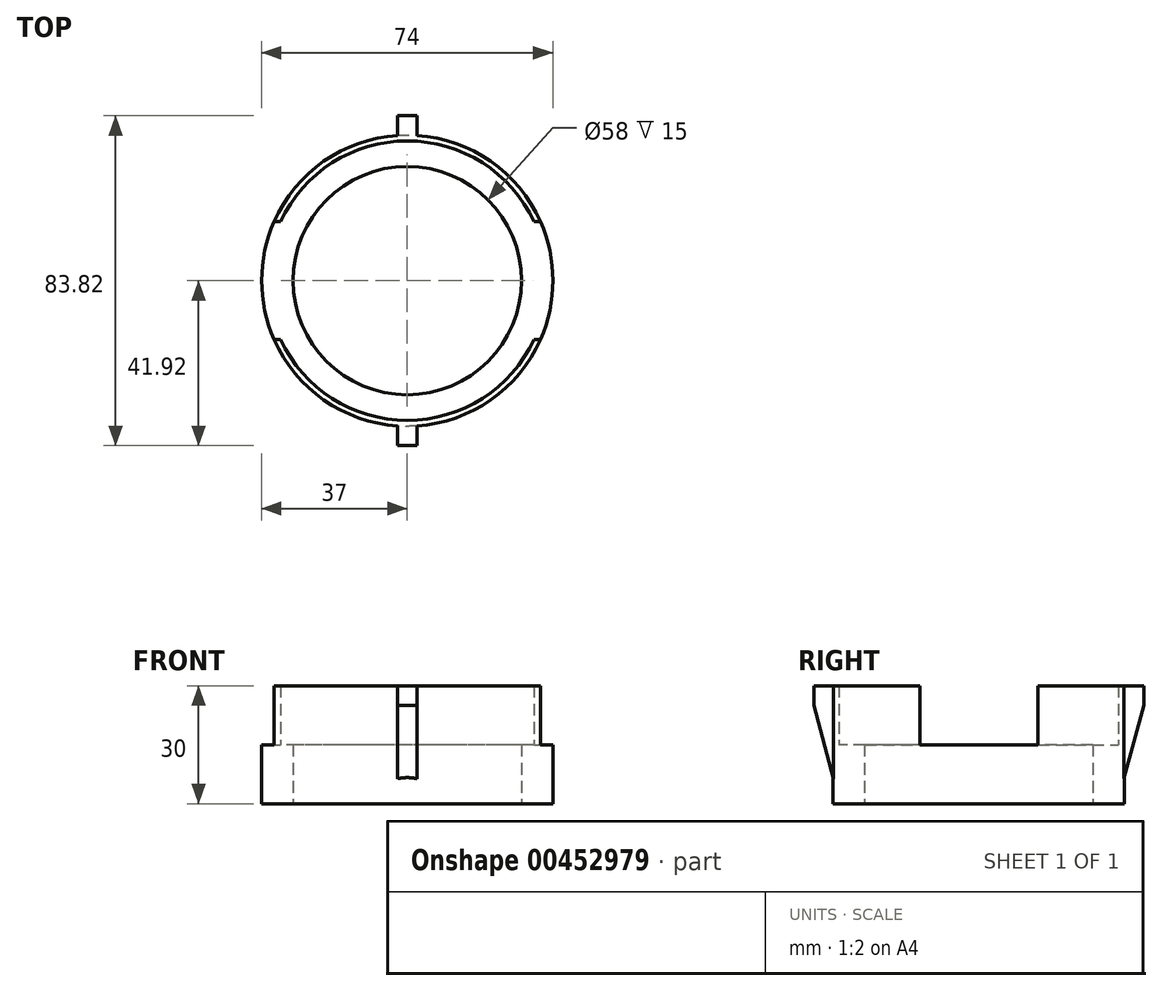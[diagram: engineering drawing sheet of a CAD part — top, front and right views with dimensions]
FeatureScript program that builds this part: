
annotation { "Feature Type Name" : "Feature", "Feature Type Description" : "" }
export const myFeature = defineFeature(function(context is Context, id is Id, definition is map)
    precondition{}
    {
        {
            var Q0;
            Q0=qCreatedBy(makeId("Top.planeOp"),FACE);
            var sketch = newSketch(context, id + "F0", { "sketchPlane" : qUnion([Q0])});
            skCircle(sketch, "E0", {"center": v(0, 0) * mm, "radius": 37 * mm});
            skCircle(sketch, "E1", {"center": v(0, 0) * mm, "radius": 35.5 * mm});
            skSolve(sketch);
        }
        {
            var Q0;
            Q0 = qSketchRegion(id + "F0", true);
            extrude(context, id + "F1", {"entities" : qUnion([Q0]), "depth" : 30 * mm});
        }
        {
            var Q0;
            Q0=qCreatedBy(makeId("Top.planeOp"),FACE);
            var sketch = newSketch(context, id + "F2", { "sketchPlane" : qUnion([Q0])});
            skLineSegment(sketch, "E2.bottom", {"start": v(-50, -15) * mm, "end": v(50, -15) * mm});
            skLineSegment(sketch, "E2.top", {"start": v(-50, 15) * mm, "end": v(50, 15) * mm});
            skLineSegment(sketch, "E2.left", {"start": v(-50, -15) * mm, "end": v(-50, 15) * mm});
            skLineSegment(sketch, "E2.right", {"start": v(50, -15) * mm, "end": v(50, 15) * mm});
            skPoint(sketch, "E2.middle", {"position": v(0, 0) * mm});
            skSolve(sketch);
        }
        {
            var Q0;
            Q0 = qSketchRegion(id + "F2", true);
            extrude(context, id + "F3", {"entities" : qUnion([Q0]), "depth" : 15 * mm});
        }
        {
            var Q0;
            Q0=makeQuery(id+"F3.opExtrude","SWEPT_BODY",BODY,{"disambiguationData":[OSD([sQuery(id+"F2.wireOp",EDGE,"E2.bottom"),sQuery(id+"F2.wireOp",EDGE,"E2.top"),sQuery(id+"F2.wireOp",EDGE,"E2.left"),sQuery(id+"F2.wireOp",EDGE,"E2.right")])]});
            transform(context, id + "F4", {"entities" : qUnion([Q0]), "transformType" : TransformType.TRANSLATION_3D, "dx" : 0 * mm, "dy" : 0 * mm, "dz" : 15 * mm, "makeCopy" : false});
        }
        {
            var Q0;
            Q0=makeQuery(id+"F3.opExtrude","SWEPT_BODY",BODY,{"disambiguationData":[OSD([sQuery(id+"F2.wireOp",EDGE,"E2.bottom"),sQuery(id+"F2.wireOp",EDGE,"E2.top"),sQuery(id+"F2.wireOp",EDGE,"E2.left"),sQuery(id+"F2.wireOp",EDGE,"E2.right")])]});
            var Q1;
            Q1=makeQuery(id+"F1.opExtrude","SWEPT_BODY",BODY,{"disambiguationData":[OSD([sQuery(id+"F0.wireOp",EDGE,"E0"),sQuery(id+"F0.wireOp",EDGE,"E1")])]});
            booleanBodies(context, id + "F5", {"operationType" : BooleanOperationType.SUBTRACTION, "tools" : qUnion([Q0]), "targets" : qUnion([Q1])});
        }
        {
            var Q0;
            Q0=qCreatedBy(makeId("Top.planeOp"),FACE);
            var sketch = newSketch(context, id + "F6", { "sketchPlane" : qUnion([Q0])});
            skCircle(sketch, "E3", {"center": v(0, 0) * mm, "radius": 35.5 * mm});
            skCircle(sketch, "E4", {"center": v(0, 0) * mm, "radius": 29 * mm});
            skSolve(sketch);
        }
        {
            var Q0;
            Q0 = qSketchRegion(id + "F6", true);
            extrude(context, id + "F7", {"entities" : qUnion([Q0]), "operationType" : NewBodyOperationType.ADD, "depth" : 15 * mm});
        }
        {
            var Q0;
            {var subQ0=sQuery(id+"F0.wireOp",EDGE,"E0");var subQ1=sQuery(id+"F0.wireOp",EDGE,"E1");Q0=makeQuery(id+"F5.opBoolean","SPLIT",FACE,{"disambiguationData":[TD([makeQuery(id+"F3.opExtrude","SWEPT_FACE",FACE,{"disambiguationData":[OSD([sQuery(id+"F2.wireOp",EDGE,"E2.bottom")])]})])],"derivedFrom":makeQuery(id+"F1.opExtrude","CAP_FACE",FACE,{"disambiguationData":[OSD([subQ0,subQ1])],"isStart":false})});}
            var sketch = newSketch(context, id + "F8", { "sketchPlane" : qUnion([Q0])});
            skLineSegment(sketch, "E5.top", {"start": v(-2.5, -41.92) * mm, "end": v(2.5, -41.92) * mm});
            skLineSegment(sketch, "E5.left", {"start": v(-2.5, -36.92) * mm, "end": v(-2.5, -41.92) * mm});
            skLineSegment(sketch, "E5.right", {"start": v(2.5, -36.92) * mm, "end": v(2.5, -41.92) * mm});
            skLineSegment(sketch, "E6", {"start": v(2.5, -36.92) * mm, "end": v(-2.5, -36.92) * mm});
            skSolve(sketch);
        }
        {
            var Q0;
            Q0 = qSketchRegion(id + "F8", true);
            extrude(context, id + "F9", {"entities" : qUnion([Q0]), "operationType" : NewBodyOperationType.ADD, "depth" : -25 * mm, "offsetDistance" : 25 * mm});
        }
        {
            var Q0;
            Q0=makeQuery(id+"F9.opExtrude","CAP_EDGE",EDGE,{"disambiguationData":[OSD([sQuery(id+"F8.wireOp",EDGE,"E5.top")])],"isStart":false});
            chamfer(context, id + "F10", {"entities" : qUnion([Q0]), "chamferType" : ChamferType.OFFSET_ANGLE, "width" : 20 * mm, "oppositeDirection" : false, "angle" : 15 * degree, "tangentPropagation" : true});
        }
        {
            var Q0;
            {var subQ0=sQuery(id+"F0.wireOp",EDGE,"E0");var subQ1=sQuery(id+"F0.wireOp",EDGE,"E1");Q0=makeQuery(id+"F5.opBoolean","SPLIT",FACE,{"disambiguationData":[TD([makeQuery(id+"F3.opExtrude","SWEPT_FACE",FACE,{"disambiguationData":[OSD([sQuery(id+"F2.wireOp",EDGE,"E2.top")])]})])],"derivedFrom":makeQuery(id+"F1.opExtrude","CAP_FACE",FACE,{"disambiguationData":[OSD([subQ0,subQ1])],"isStart":false})});}
            var sketch = newSketch(context, id + "F11", { "sketchPlane" : qUnion([Q0])});
            skLineSegment(sketch, "E7.bottom", {"start": v(2.5, 36.9) * mm, "end": v(-2.5, 36.9) * mm});
            skLineSegment(sketch, "E7.top", {"start": v(2.5, 41.9) * mm, "end": v(-2.5, 41.9) * mm});
            skLineSegment(sketch, "E7.left", {"start": v(2.5, 36.9) * mm, "end": v(2.5, 41.9) * mm});
            skLineSegment(sketch, "E7.right", {"start": v(-2.5, 36.9) * mm, "end": v(-2.5, 41.9) * mm});
            skSolve(sketch);
        }
        {
            var Q0;
            Q0 = qSketchRegion(id + "F11", true);
            extrude(context, id + "F12", {"entities" : qUnion([Q0]), "operationType" : NewBodyOperationType.ADD, "depth" : -25 * mm, "offsetDistance" : 25 * mm});
        }
        {
            var Q0;
            Q0=makeQuery(id+"F12.opExtrude","CAP_EDGE",EDGE,{"disambiguationData":[OSD([sQuery(id+"F11.wireOp",EDGE,"E7.top")])],"isStart":false});
            chamfer(context, id + "F13", {"entities" : qUnion([Q0]), "chamferType" : ChamferType.OFFSET_ANGLE, "width" : 20 * mm, "oppositeDirection" : false, "angle" : 15 * degree, "tangentPropagation" : true});
        }
    });
